# Revit family: НЕВАТОМ_Щит управления противопожарными клапанами ABUm-KP, Версия 1
name_source: partatom
category: Оборудование
revit_build: Autodesk Revit 2017 (Build: 20170118_1100(x64)
units: mm (PartAtom-declared; Revit-internal decimal feet)

## family parameters
Всегда вертикально = Да
На основе рабочей плоскости = Нет
Общий = Нет
При загрузке вырезать с полостями = Нет
Размер круглого соединителя = Использовать диаметр
Тип детали = Нормальный
Точка расчета площади = Нет

## types (33) — shared parameters
ADSK_Единица измерения = шт.
ADSK_Завод-изготовитель = НЕВАТОМ
ADSK_Количество = 1
ADSK_Напряжение = 220 В

## per-type parameters (varying)
| type | ADSK_Марка | ADSK_Наименование | ADSK_Размер_Высота | ADSK_Размер_Длина | ADSK_Размер_Ширина | НЕВАТОМ_Количество противопожарных клапанов | НЕВАТОМ_Номинальный ток клапанов | НЕВАТОМ_Ориентировочная мощность клапанов |
| ABUm-KP-EM220(24)/1 | ABUm-KP-EM220(24)/1 | ABUm-KP-EM220(24)/1 | 600 мм | 400 мм | 200 мм | 1 | 0 А | 0 кВт |
| ABUm-KP-EM220(24)/2 | ABUm-KP-EM220(24)/2 | ABUm-KP-EM220(24)/2 | 600 мм | 400 мм | 200 мм | 2 | 0 А | 0 кВт |
| ABUm-KP-EM220(24)/4 | ABUm-KP-EM220(24)/4 | ABUm-KP-EM220(24)/4 | 800 мм | 600 мм | 200 мм | 4 | 2 А | 0 кВт |
| ABUm-KP-EM220(24)/6 | ABUm-KP-EM220(24)/6 | ABUm-KP-EM220(24)/6 | 800 мм | 600 мм | 200 мм | 6 | 2 А | 0 кВт |
| ABUm-KP-EM220(24)/8 | ABUm-KP-EM220(24)/8 | ABUm-KP-EM220(24)/8 | 800 мм | 600 мм | 200 мм | 8 | 4 А | 1 кВт |
| ABUm-KP-EM220(24)/10 | ABUm-KP-EM220(24)/10 | ABUm-KP-EM220(24)/10 | 800 мм | 600 мм | 200 мм | 10 | 4 А | 1 кВт |
| ABUm-KP-EM220(24)/12 | ABUm-KP-EM220(24)/12 | ABUm-KP-EM220(24)/12 | 800 мм | 600 мм | 200 мм | 12 | 5 А | 1 кВт |
| ABUm-KP-EM220(24)/14 | ABUm-KP-EM220(24)/14 | ABUm-KP-EM220(24)/14 | 1000 мм | 800 мм | 300 мм | 14 | 6 А | 1 кВт |
| ABUm-KP-EM220(24)/16 | ABUm-KP-EM220(24)/16 | ABUm-KP-EM220(24)/16 | 1000 мм | 800 мм | 300 мм | 16 | 6 А | 1 кВт |
| ABUm-KP-EM220(24)/18 | ABUm-KP-EM220(24)/18 | ABUm-KP-EM220(24)/18 | 1000 мм | 800 мм | 300 мм | 18 | 7 А | 1 кВт |
| ABUm-KP-EM220(24)/20 | ABUm-KP-EM220(24)/20 | ABUm-KP-EM220(24)/20 | 1000 мм | 800 мм | 300 мм | 20 | 8 А | 1 кВт |
| ABUm-KP-MR220(24)/1 | ABUm-KP-MR220(24)/1 | ABUm-KP-MR220(24)/1 | 600 мм | 400 мм | 200 мм | 1 | 0 А | 4 кВт |
| ABUm-KP-MR220(24)/2 | ABUm-KP-MR220(24)/2 | ABUm-KP-MR220(24)/2 | 600 мм | 400 мм | 200 мм | 2 | 0 А | 8 кВт |
| ABUm-KP-MR220(24)/4 | ABUm-KP-MR220(24)/4 | ABUm-KP-MR220(24)/4 | 800 мм | 600 мм | 200 мм | 4 | 0 А | 17 кВт |
| ABUm-KP-MR220(24)/6 | ABUm-KP-MR220(24)/6 | ABUm-KP-MR220(24)/6 | 800 мм | 600 мм | 200 мм | 6 | 0 А | 25 кВт |
| ABUm-KP-MR220(24)/8 | ABUm-KP-MR220(24)/8 | ABUm-KP-MR220(24)/8 | 800 мм | 600 мм | 200 мм | 8 | 34 А | 0 кВт |
| ABUm-KP-MR220(24)/10 | ABUm-KP-MR220(24)/10 | ABUm-KP-MR220(24)/10 | 800 мм | 600 мм | 200 мм | 10 | 0 А | 42 кВт |
| ABUm-KP-MR220(24)/12 | ABUm-KP-MR220(24)/12 | ABUm-KP-MR220(24)/12 | 800 мм | 600 мм | 200 мм | 12 | 0 А | 50 кВт |
| ABUm-KP-MR220(24)/14 | ABUm-KP-MR220(24)/14 | ABUm-KP-MR220(24)/14 | 1000 мм | 800 мм | 300 мм | 14 | 0 А | 59 кВт |
| ABUm-KP-MR220(24)/16 | ABUm-KP-MR220(24)/16 | ABUm-KP-MR220(24)/16 | 1000 мм | 800 мм | 300 мм | 16 | 0 А | 67 кВт |
| ABUm-KP-MR220(24)/18 | ABUm-KP-MR220(24)/18 | ABUm-KP-MR220(24)/18 | 1000 мм | 800 мм | 300 мм | 18 | 0 А | 76 кВт |
| ABUm-KP-MR220(24)/20 | ABUm-KP-MR220(24)/20 | ABUm-KP-MR220(24)/20 | 1000 мм | 800 мм | 300 мм | 20 | 0 А | 84 кВт |
| ABUm-KP-MP220(24)/1 | ABUm-KP-MP220(24)/1 | ABUm-KP-MP220(24)/1 | 600 мм | 400 мм | 200 мм | 1 | 0 А | 4 кВт |
| ABUm-KP-MP220(24)/2 | ABUm-KP-MP220(24)/1 | ABUm-KP-MP220(24)/1 | 600 мм | 400 мм | 200 мм | 2 | 0 А | 8 кВт |
| ABUm-KP-MP220(24)/4 | ABUm-KP-MP220(24)/4 | ABUm-KP-MP220(24)/4 | 800 мм | 600 мм | 200 мм | 4 | 0 А | 17 кВт |
| ABUm-KP-MP220(24)/6 | ABUm-KP-MP220(24)/6 | ABUm-KP-MP220(24)/6 | 800 мм | 600 мм | 200 мм | 6 | 0 А | 25 кВт |
| ABUm-KP-MP220(24)/8 | ABUm-KP-MP220(24)/8 | ABUm-KP-MP220(24)/8 | 800 мм | 600 мм | 200 мм | 8 | 0 А | 34 кВт |
| ABUm-KP-MP220(24)/10 | ABUm-KP-MP220(24)/10 | ABUm-KP-MP220(24)/10 | 800 мм | 600 мм | 200 мм | 10 | 0 А | 42 кВт |
| ABUm-KP-MP220(24)/12 | ABUm-KP-MP220(24)/12 | ABUm-KP-MP220(24)/12 | 800 мм | 600 мм | 200 мм | 12 | 0 А | 50 кВт |
| ABUm-KP-MP220(24)/14 | ABUm-KP-MP220(24)/14 | ABUm-KP-MP220(24)/14 | 1000 мм | 800 мм | 300 мм | 14 | 0 А | 59 кВт |
| ABUm-KP-MP220(24)/16 | ABUm-KP-MP220(24)/16 | ABUm-KP-MP220(24)/16 | 1000 мм | 800 мм | 300 мм | 16 | 0 А | 67 кВт |
| ABUm-KP-MP220(24)/18 | ABUm-KP-MP220(24)/18 | ABUm-KP-MP220(24)/18 | 1000 мм | 800 мм | 300 мм | 18 | 0 А | 76 кВт |
| ABUm-KP-MP220(24)/20 | ABUm-KP-MP220(24)/20 | ABUm-KP-MP220(24)/20 | 1000 мм | 800 мм | 300 мм | 20 | 0 А | 84 кВт |
